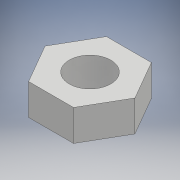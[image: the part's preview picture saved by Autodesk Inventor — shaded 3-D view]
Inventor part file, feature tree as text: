
AUTODESK INVENTOR PART (.ipt)
format: ipt  version: 2018.3 (Build 223284000, 284)  size: 97,792 bytes
history: native  units: mm
features: extrude x1, sketch x1
ambient origin geometry x8: Origin, YZ Plane, XZ Plane, XY Plane, X Axis, Y Axis, Z Axis, Center Point
bodies: Solid1 (feature_tree)
feature tree (2):
  extrude  "Extrusion1"  Depth=3.0mm
  sketch  "Sketch1"  dims[d0=7.5mm d1=4.0mm d2=3.0mm d3=0.0mm]
